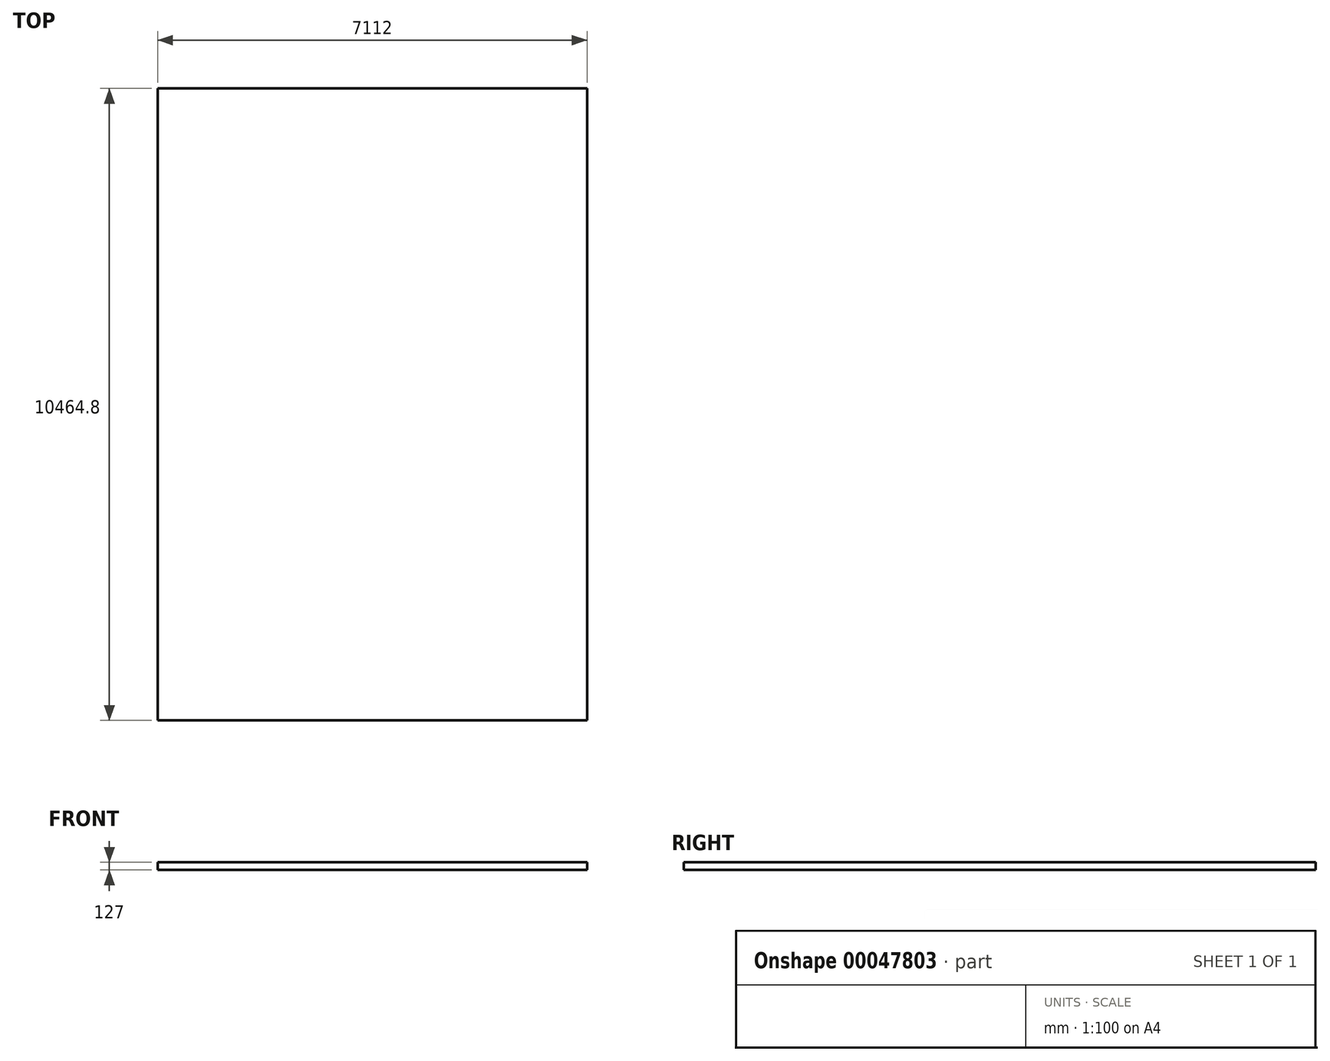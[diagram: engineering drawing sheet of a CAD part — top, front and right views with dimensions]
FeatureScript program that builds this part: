
annotation { "Feature Type Name" : "Feature", "Feature Type Description" : "" }
export const myFeature = defineFeature(function(context is Context, id is Id, definition is map)
    precondition{}
    {
        {
            var Q0;
            Q0=qCreatedBy(makeId("Top.planeOp"),FACE);
            var sketch = newSketch(context, id + "F0", { "sketchPlane" : qUnion([Q0])});
            skLineSegment(sketch, "E0.bottom", {"start": v(3556, 5232.4) * mm, "end": v(-3556, 5232.4) * mm});
            skLineSegment(sketch, "E0.top", {"start": v(3556, -5232.4) * mm, "end": v(-3556, -5232.4) * mm});
            skLineSegment(sketch, "E0.left", {"start": v(3556, 5232.4) * mm, "end": v(3556, -5232.4) * mm});
            skLineSegment(sketch, "E0.right", {"start": v(-3556, 5232.4) * mm, "end": v(-3556, -5232.4) * mm});
            skPoint(sketch, "E0.middle", {"position": v(0, 0) * mm});
            skSolve(sketch);
        }
        {
            var Q0;
            Q0=makeQuery(id+"F0.imprint","IMPRINT",FACE,{"disambiguationData":[TD([[makeQuery(id+"F0.imprint","IMPRINT",EDGE,{"derivedFrom":sQuery(id+"F0.wireOp",EDGE,"E0.bottom")}),1.0]])]});
            extrude(context, id + "F1", {"entities" : qUnion([Q0]), "depth" : 127 * mm});
        }
    });
